# Revit family: Accessory-Shroud-KOHLER-Brenham-K-1998
name_source: partatom
category: Specialty Equipment
units: mm (PartAtom-declared; Revit-internal decimal feet)

## family parameters
Cut with Voids When Loaded = No
Host = Face
OmniClass Number = 23.31.25.00
OmniClass Title = Toilet and Bath Specialties
Part Type = Normal
Room Calculation Point = No
Round Connector Dimension = Use Diameter
Shared = No

## types (4) — shared parameters
ADA Compliant = Yes
Assembly Code = C1030200
Date Modified = 05/02/2023
Default Elevation = 28"
Description = Shroud
Height = 10 1/2"
Length = 10 5/8"
Manufacturer = Kohler Co.
Master Format 2014 = 10 28 00
Master Format 2014 Name = Toilet, Bath, and Laundry Accessories
Material = Vitreous China
Product Documentation Link = https://www.us.kohler.com
Product Name = Brenham
Product Page URL = http://www.us.kohler.com
URL = https://www.us.kohler.com
WaterSense Certified = No
Width = 9 3/4"

## per-type parameters (varying)
| type | Finish | Model | Type |
| 0-White | Kohler-Vitreous_China-0-White | K-1998-0 | 1 |
| 7-Black Black | Kohler-Vitreous_China-7-Black_Black | K-1998-7 | 2 |
| 96-Biscuit | Kohler-Vitreous_China-96-Biscuit | K-1998-96 | 3 |
| SS, 0-White | Kohler-Vitreous_China-0-White | K-1998-SS-0 | 4 |

## geometry (parser evidence)
native form markers: Sweep x5
no freeform markers — native parametric forms only
